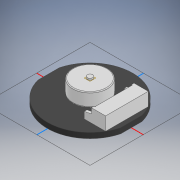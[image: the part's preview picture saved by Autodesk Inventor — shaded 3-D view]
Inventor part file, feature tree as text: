
AUTODESK INVENTOR PART (.ipt)
format: ipt  version: 2022 (Build 260153000, 153)  size: 190,464 bytes
history: native  units: mm
features: extrude x5, sketch x5, other x2, fillet x1, mirror x1
ambient origin geometry x8: Origin, YZ Plane, XZ Plane, XY Plane, X Axis, Y Axis, Z Axis, Center Point
bodies: Body1 (feature_tree)
feature tree (14):
  other  "Твердое тело1"
  extrude  "Выдавливание1"  Depth=32.0mm
  extrude  "Выдавливание2"  Depth=15.5mm
  other  "РабПлоскость1"
  extrude  "Выдавливание3"  Depth=15.5mm
  fillet  "Сопряжение1"  Radius=2.0mm
  extrude  "Выдавливание4"  Depth=2.0mm
  extrude  "Выдавливание6"  Depth=7.0mm TaperAngle=0.0deg
  mirror  "Зеркальное отражение1"
  sketch  "Эскиз1"
  sketch  "Эскиз2"
  sketch  "Эскиз3"
  sketch  "Эскиз4"
  sketch  "Эскиз6"
